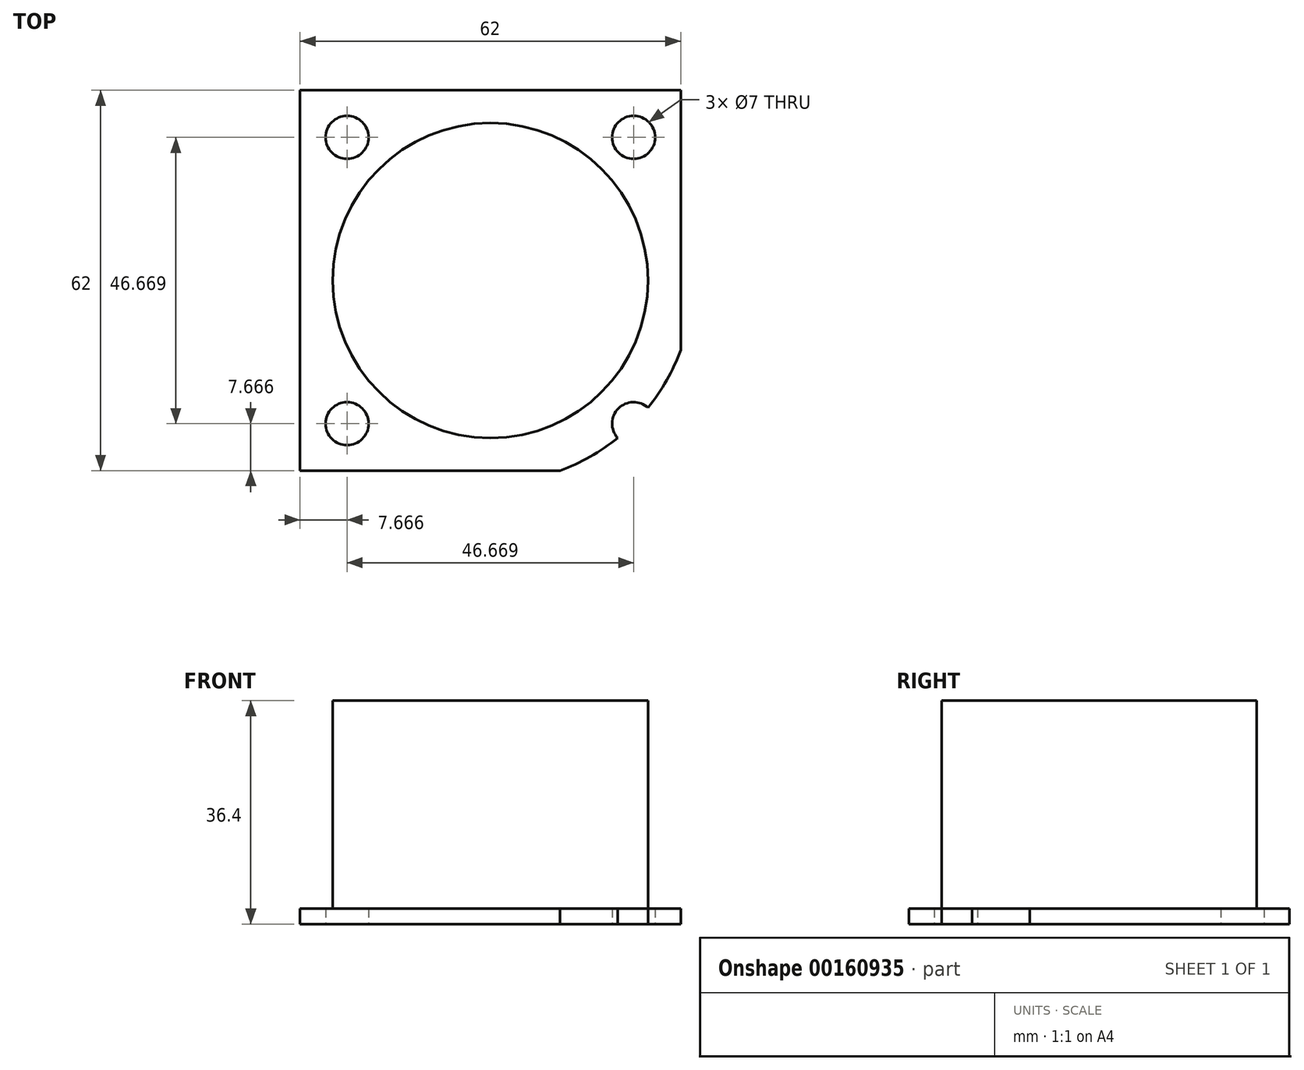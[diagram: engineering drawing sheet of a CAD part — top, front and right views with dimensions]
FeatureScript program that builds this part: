
annotation { "Feature Type Name" : "Feature", "Feature Type Description" : "" }
export const myFeature = defineFeature(function(context is Context, id is Id, definition is map)
    precondition{}
    {
        {
            var Q0;
            Q0=qCreatedBy(makeId("Top.planeOp"),FACE);
            var sketch = newSketch(context, id + "F0", { "sketchPlane" : qUnion([Q0])});
            skCircle(sketch, "E0", {"center": v(0, 0) * mm, "radius": 33 * mm});
            skLineSegment(sketch, "E1", {"start": v(-63.1, 0) * mm, "end": v(73.24, 0) * mm, "construction": true});
            skLineSegment(sketch, "E2", {"start": v(-53.04, -53.04) * mm, "end": v(49.13, 49.13) * mm, "construction": true});
            skPoint(sketch, "E3", {"position": v(23.33, 23.33) * mm});
            skCircle(sketch, "E4", {"center": v(23.33, 23.33) * mm, "radius": 3.5 * mm});
            skCircle(sketch, "E5.MirrorC", {"center": v(23.33, -23.33) * mm, "radius": 3.5 * mm});
            skCircle(sketch, "E6.MirrorC", {"center": v(-23.33, 23.33) * mm, "radius": 3.5 * mm});
            skCircle(sketch, "E7.MirrorC", {"center": v(-23.33, -23.33) * mm, "radius": 3.5 * mm});
            skLineSegment(sketch, "E8.bottom", {"start": v(31, 31) * mm, "end": v(-31, 31) * mm});
            skLineSegment(sketch, "E8.top", {"start": v(31, -31) * mm, "end": v(-31, -31) * mm});
            skLineSegment(sketch, "E8.left", {"start": v(31, 31) * mm, "end": v(31, -31) * mm});
            skLineSegment(sketch, "E8.right", {"start": v(-31, 31) * mm, "end": v(-31, -31) * mm});
            skCircle(sketch, "E9", {"center": v(0, 0) * mm, "radius": 25.67 * mm});
            skSolve(sketch);
        }
        {
            var Q0;
            {var subQ1=sQuery(id+"F0.wireOp",EDGE,"E8.bottom");var subQ3=sQuery(id+"F0.wireOp",EDGE,"E0");var subQ4=makeQuery(id+"F0.imprint","INTERSECT",VERTEX,{"disambiguationData":[OD(1.0)],"derivedFrom":[subQ3,subQ1]});Q0=makeQuery(id+"F0.imprint","IMPRINT",FACE,{"disambiguationData":[TD([[makeQuery(id+"F0.imprint","IMPRINT",EDGE,{"disambiguationData":[TD([[subQ4,-1.0]])],"derivedFrom":subQ3}),-1.0]])]});}
            var Q1;
            Q1=makeQuery(id+"F0.imprint","IMPRINT",FACE,{"disambiguationData":[TD([[makeQuery(id+"F0.imprint","IMPRINT",EDGE,{"derivedFrom":sQuery(id+"F0.wireOp",EDGE,"E9")}),-1.0]])]});
            var Q2;
            {var subQ0=sQuery(id+"F0.wireOp",EDGE,"E8.right");var subQ3=sQuery(id+"F0.wireOp",EDGE,"E0");var subQ8=makeQuery(id+"F0.imprint","INTERSECT",VERTEX,{"disambiguationData":[OD(1.0)],"derivedFrom":[subQ3,subQ0]});Q2=makeQuery(id+"F0.imprint","IMPRINT",FACE,{"disambiguationData":[TD([[makeQuery(id+"F0.imprint","IMPRINT",EDGE,{"disambiguationData":[TD([[subQ8,-1.0]])],"derivedFrom":subQ3}),-1.0]])]});}
            var Q3;
            {var subQ1=sQuery(id+"F0.wireOp",EDGE,"E0");var subQ5=sQuery(id+"F0.wireOp",EDGE,"E8.top");var subQ7=makeQuery(id+"F0.imprint","INTERSECT",VERTEX,{"disambiguationData":[OD(1.0)],"derivedFrom":[subQ1,subQ5]});Q3=makeQuery(id+"F0.imprint","IMPRINT",FACE,{"disambiguationData":[TD([[makeQuery(id+"F0.imprint","IMPRINT",EDGE,{"disambiguationData":[TD([[subQ7,-1.0]])],"derivedFrom":subQ1}),-1.0]])]});}
            var Q4;
            {var subQ0=sQuery(id+"F0.wireOp",EDGE,"E8.left");var subQ3=sQuery(id+"F0.wireOp",EDGE,"E0");var subQ8=makeQuery(id+"F0.imprint","INTERSECT",VERTEX,{"disambiguationData":[OD(0.0)],"derivedFrom":[subQ3,subQ0]});Q4=makeQuery(id+"F0.imprint","IMPRINT",FACE,{"disambiguationData":[TD([[makeQuery(id+"F0.imprint","IMPRINT",EDGE,{"disambiguationData":[TD([[subQ8,-1.0]])],"derivedFrom":subQ3}),-1.0]])]});}
            extrude(context, id + "F1", {"entities" : qUnion([Q0, Q1, Q2, Q3, Q4]), "depth" : 2.54 * mm});
        }
        {
            var Q0;
            Q0=makeQuery(id+"F0.imprint","IMPRINT",FACE,{"disambiguationData":[TD([[makeQuery(id+"F0.imprint","IMPRINT",EDGE,{"derivedFrom":sQuery(id+"F0.wireOp",EDGE,"E9")}),1.0]])]});
            extrude(context, id + "F2", {"entities" : qUnion([Q0]), "operationType" : NewBodyOperationType.ADD, "depth" : 36.4 * mm});
        }
    });
